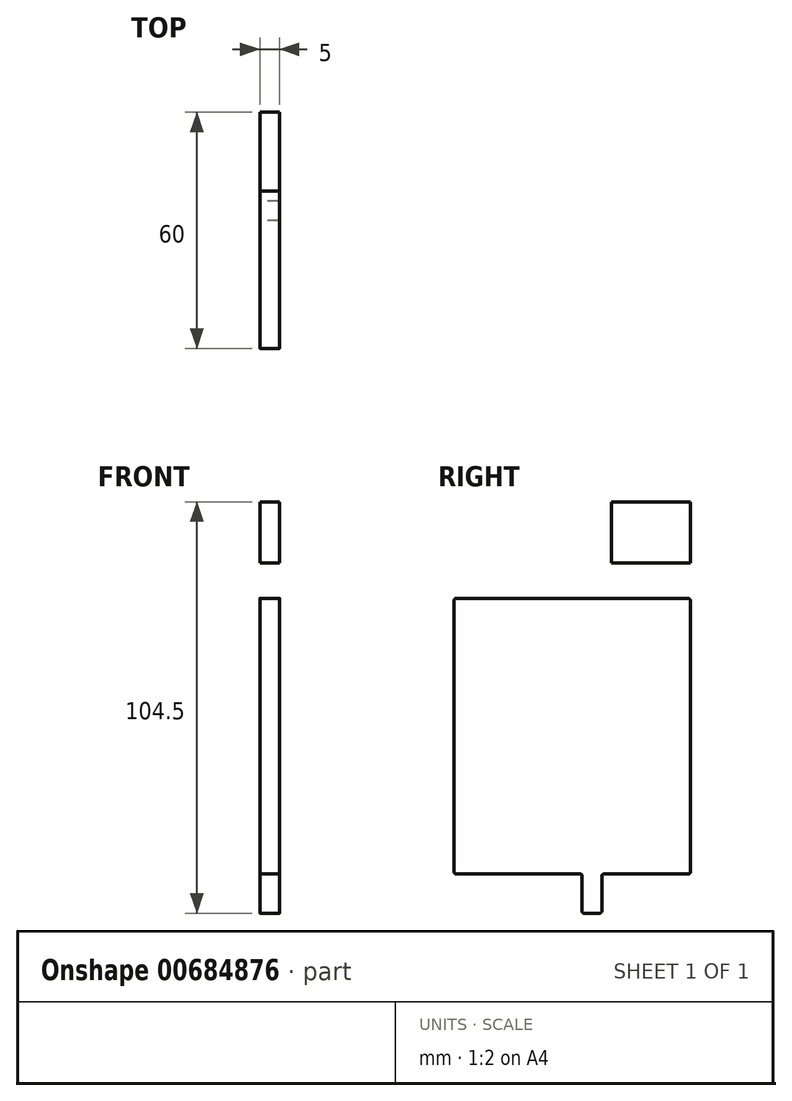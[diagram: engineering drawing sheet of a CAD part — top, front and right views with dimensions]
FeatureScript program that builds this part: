
annotation { "Feature Type Name" : "Feature", "Feature Type Description" : "" }
export const myFeature = defineFeature(function(context is Context, id is Id, definition is map)
    precondition{}
    {
        {
            var Q0;
            Q0=qCreatedBy(makeId("Right.planeOp"),FACE);
            var sketch = newSketch(context, id + "F0", { "sketchPlane" : qUnion([Q0])});
            skLineSegment(sketch, "E0", {"start": v(0, 0) * mm, "end": v(0, -70) * mm});
            skLineSegment(sketch, "E1", {"start": v(0, -70) * mm, "end": v(12.4, -70) * mm});
            skLineSegment(sketch, "E2.0", {"start": v(37.5, -70.04) * mm, "end": v(37.5, -81.07) * mm});
            skLineSegment(sketch, "E3", {"start": v(12, -70) * mm, "end": v(12.4, -70) * mm});
            skLineSegment(sketch, "E4", {"start": v(0, -70) * mm, "end": v(12, -70) * mm});
            skLineSegment(sketch, "E5", {"start": v(32.5, -80) * mm, "end": v(32.5, -70) * mm});
            skPoint(sketch, "E6.trimOffspring.start.orphan", {"position": v(25, -70) * mm});
            skLineSegment(sketch, "E7", {"start": v(37.5, -80) * mm, "end": v(37.5, -81.07) * mm});
            skLineSegment(sketch, "E8", {"start": v(32.5, -80) * mm, "end": v(37.5, -80) * mm});
            skLineSegment(sketch, "E9", {"start": v(11.37, -27.14) * mm, "end": v(11.37, -26.74) * mm});
            skLineSegment(sketch, "E10", {"start": v(38.63, -27.14) * mm, "end": v(38.63, -26.74) * mm});
            skLineSegment(sketch, "E11", {"start": v(0, -70) * mm, "end": v(32.5, -70) * mm});
            skLineSegment(sketch, "E12.trimOffspring", {"start": v(32.5, -70) * mm, "end": v(0, -70) * mm});
            skLineSegment(sketch, "E13.0", {"start": v(60, -0.04) * mm, "end": v(60, -70.04) * mm});
            skLineSegment(sketch, "E14", {"start": v(60, -70.04) * mm, "end": v(37.5, -70.04) * mm});
            skLineSegment(sketch, "E15.0", {"start": v(42.5, 9) * mm, "end": v(40, 9) * mm});
            skPoint(sketch, "E16.orphan", {"position": v(42.5, 0) * mm});
            skLineSegment(sketch, "E17", {"start": v(40, 24.5) * mm, "end": v(42.5, 24.5) * mm});
            skPoint(sketch, "E17.startSnap0", {"position": v(42.5, 24.5) * mm});
            skPoint(sketch, "E17.endSnap0", {"position": v(42.5, 24.5) * mm});
            skPoint(sketch, "E18.end.orphan", {"position": v(42.5, 40) * mm});
            skLineSegment(sketch, "E19", {"start": v(60, 9) * mm, "end": v(60, 24.5) * mm});
            skLineSegment(sketch, "E20", {"start": v(42.5, 24.5) * mm, "end": v(60, 24.5) * mm});
            skLineSegment(sketch, "E21", {"start": v(42.5, 9) * mm, "end": v(60, 9) * mm});
            skPoint(sketch, "E22.orphan", {"position": v(22.5, 24.5) * mm});
            skLineSegment(sketch, "E23.0", {"start": v(40, 9) * mm, "end": v(40, 24.5) * mm});
            skLineSegment(sketch, "E24", {"start": v(0, 0) * mm, "end": v(60, -0.04) * mm});
            skSolve(sketch);
        }
        {
            var Q0;
            {var subQ1=sQuery(id+"F0.wireOp",EDGE,"E0");Q0=makeQuery(id+"F0.imprint","IMPRINT",FACE,{"disambiguationData":[TD([[makeQuery(id+"F0.imprint","IMPRINT",EDGE,{"derivedFrom":subQ1}),1.0]])]});}
            var Q1;
            Q1=makeQuery(id+"F0.imprint","IMPRINT",FACE,{"disambiguationData":[TD([[makeQuery(id+"F0.imprint","IMPRINT",EDGE,{"derivedFrom":sQuery(id+"F0.wireOp",EDGE,"KUJi0EKv-68yc-6Nkf-644W-VpfIH1upkmh2")}),-1.0]])]});
            var Q2;
            Q2=makeQuery(id+"F0.imprint","IMPRINT",FACE,{"disambiguationData":[TD([[makeQuery(id+"F0.imprint","IMPRINT",EDGE,{"derivedFrom":sQuery(id+"F0.wireOp",EDGE,"E15.0")}),-1.0]])]});
            extrude(context, id + "F1", {"entities" : qUnion([Q0, Q1, Q2]), "depth" : 5 * mm, "offsetDistance" : 25 * mm});
        }
        {
            var Q0;
            Q0=makeQuery(id+"F1.opExtrude","SWEPT_EDGE",EDGE,{"disambiguationData":[OSD([sQuery(id+"F0.wireOp",EDGE,"E0"),sQuery(id+"F0.wireOp",EDGE,"E24")])]});
            var Q1;
            Q1=makeQuery(id+"F1.opExtrude","SWEPT_EDGE",EDGE,{"disambiguationData":[OSD([sQuery(id+"F0.wireOp",EDGE,"E0"),sQuery(id+"F0.wireOp",EDGE,"E12.trimOffspring")])]});
            var Q2;
            Q2=makeQuery(id+"F1.opExtrude","SWEPT_EDGE",EDGE,{"disambiguationData":[OSD([sQuery(id+"F0.wireOp",EDGE,"E13.0"),sQuery(id+"F0.wireOp",EDGE,"E14")])]});
            var Q3;
            Q3=makeQuery(id+"F1.opExtrude","SWEPT_EDGE",EDGE,{"disambiguationData":[OSD([sQuery(id+"F0.wireOp",EDGE,"E13.0"),sQuery(id+"F0.wireOp",EDGE,"E24")])]});
            fillet(context, id + "F2", {"entities" : qUnion([Q0, Q1, Q2, Q3]), "radius" : 0.5 * mm, "tangentPropagation" : true, "allowEdgeOverflow" : false});
        }
        {
            var Q0;
            Q0=makeQuery(id+"F1.opExtrude","SWEPT_EDGE",EDGE,{"disambiguationData":[OSD([sQuery(id+"F0.wireOp",EDGE,"E2.0"),sQuery(id+"F0.wireOp",EDGE,"E14")])]});
            var Q1;
            Q1=makeQuery(id+"F1.opExtrude","SWEPT_EDGE",EDGE,{"disambiguationData":[OSD([sQuery(id+"F0.wireOp",EDGE,"E5"),sQuery(id+"F0.wireOp",EDGE,"E12.trimOffspring")])]});
            fillet(context, id + "F3", {"entities" : qUnion([Q0, Q1]), "radius" : 0.5 * mm, "tangentPropagation" : true, "allowEdgeOverflow" : false});
        }
        {
            var Q0;
            Q0=makeQuery(id+"F1.opExtrude","SWEPT_EDGE",EDGE,{"disambiguationData":[OSD([sQuery(id+"F0.wireOp",EDGE,"E5"),sQuery(id+"F0.wireOp",EDGE,"E8")])]});
            var Q1;
            Q1=makeQuery(id+"F1.opExtrude","SWEPT_EDGE",EDGE,{"disambiguationData":[OSD([sQuery(id+"F0.wireOp",EDGE,"E2.0"),sQuery(id+"F0.wireOp",EDGE,"E8")])]});
            fillet(context, id + "F4", {"entities" : qUnion([Q0, Q1]), "radius" : 0.5 * mm, "tangentPropagation" : true, "allowEdgeOverflow" : false});
        }
    });
